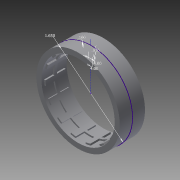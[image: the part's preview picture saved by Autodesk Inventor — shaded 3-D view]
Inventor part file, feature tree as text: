
AUTODESK INVENTOR PART (.ipt)
format: ipt  version: 2015 (Build 190159000, 159)  size: 216,064 bytes
history: native  units: in
note: dims shown in document units (in); Inventor stores cm internally (conversion verified against a paired STEP export)
features: extrude x3, sketch x2, pattern_circular x1, plane x1
ambient origin geometry x8: Origin, YZ Plane, XZ Plane, XY Plane, X Axis, Y Axis, Z Axis, Center Point
bodies: Solid1 (feature_tree)
feature tree (7):
  sketch  "Sketch1"  dims[d0=1.65in d1=0.1in]
  extrude  "Extrusion1"  Depth=0.1in
  extrude  "Extrusion2"  Depth=0.05in
  pattern_circular  "Circular Pattern1"  [2 undecoded]
  plane  "Work Plane1"
  extrude  "Extrusion3"  Depth=0.05in
  sketch  "Sketch2"  dims[d2=0.03in d3=0.0275in d4=0.0275in d5=0.0275in d6=0.5in d7=0.0in d8=0.4in d9=0.0in d10=5.9055in d11=360.0deg d13=0.05in d14=0.0in]
note: 2 required parameter values undecoded (feature->parameter linkage not recoverable at this tier; creation-order binding heuristic only, values carry confidence <= 0.55)
